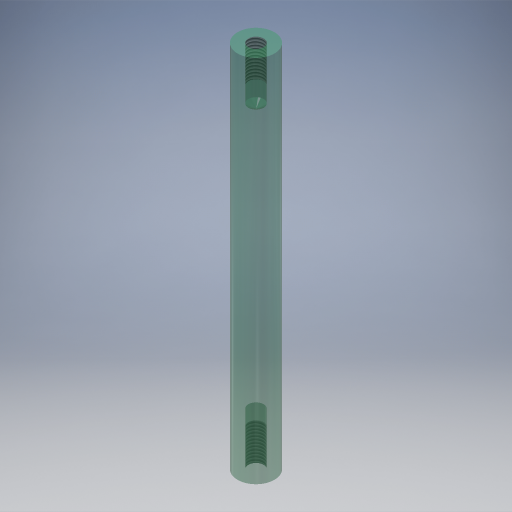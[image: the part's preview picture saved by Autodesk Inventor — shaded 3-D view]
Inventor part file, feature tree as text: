
AUTODESK INVENTOR PART (.ipt)
format: ipt  version: 2024.3 (Build 283343000, 343)  size: 292,864 bytes
history: native  units: mm
features: hole x2, sketch x2, extrude x1
ambient origin geometry x8: Origin, YZ Plane, XZ Plane, XY Plane, X Axis, Y Axis, Z Axis, Center Point
bodies: Volumenkörper1 (feature_tree)
feature tree (5):
  extrude  "Extrusion1"  Depth=100.0mm TaperAngle=0.0deg
  hole  "Bohrung1"  [1 undecoded]
  hole  "Bohrung2"  [1 undecoded]
  sketch  "Skizze2"  dims[d0=10.0mm d1=100.0mm d2=0.0mm]
  sketch  "Skizze3"  dims[d3=4.134mm d4=10.0mm d5=4.0mm d6=2.0mm d7=90.0deg d8=14.2mm d9=20.594885mm d10=4.134mm d11=10.0mm d12=4.0mm d13=2.0mm d14=90.0deg d15=14.2mm d16=20.594885mm]
note: 2 required parameter values undecoded (feature->parameter linkage not recoverable at this tier; creation-order binding heuristic only, values carry confidence <= 0.55)
